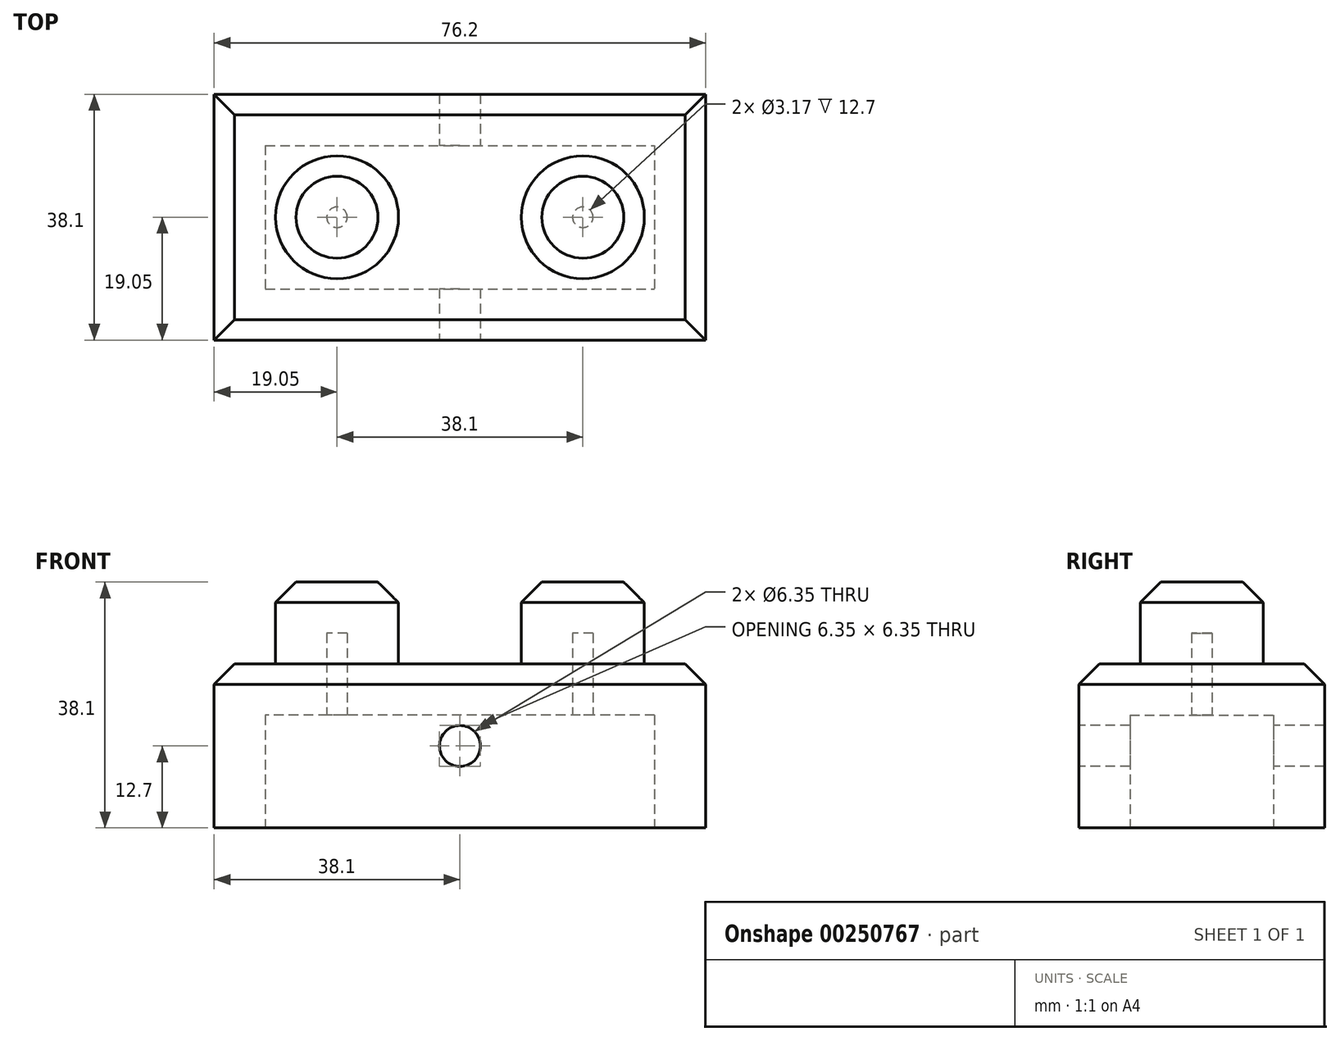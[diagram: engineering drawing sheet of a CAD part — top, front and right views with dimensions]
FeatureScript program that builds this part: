
annotation { "Feature Type Name" : "Feature", "Feature Type Description" : "" }
export const myFeature = defineFeature(function(context is Context, id is Id, definition is map)
    precondition{}
    {
        {
            var Q0;
            Q0=qCreatedBy(makeId("Top.planeOp"),FACE);
            var sketch = newSketch(context, id + "F0", { "sketchPlane" : qUnion([Q0])});
            skLineSegment(sketch, "E0.bottom", {"start": v(0, 0) * mm, "end": v(76.2, 0) * mm});
            skLineSegment(sketch, "E0.top", {"start": v(0, -38.1) * mm, "end": v(76.2, -38.1) * mm});
            skLineSegment(sketch, "E0.left", {"start": v(0, 0) * mm, "end": v(0, -38.1) * mm});
            skLineSegment(sketch, "E0.right", {"start": v(76.2, 0) * mm, "end": v(76.2, -38.1) * mm});
            skSolve(sketch);
        }
        {
            var Q0;
            Q0=makeQuery(id+"F0.imprint","IMPRINT",FACE,{"disambiguationData":[TD([[makeQuery(id+"F0.imprint","IMPRINT",EDGE,{"derivedFrom":sQuery(id+"F0.wireOp",EDGE,"E0.bottom")}),-1.0]])]});
            extrude(context, id + "F1", {"entities" : qUnion([Q0]), "depth" : 25.4 * mm});
        }
        {
            var Q0;
            Q0=makeQuery(id+"F1.opExtrude","CAP_FACE",FACE,{"disambiguationData":[OSD([sQuery(id+"F0.wireOp",EDGE,"E0.bottom"),sQuery(id+"F0.wireOp",EDGE,"E0.top"),sQuery(id+"F0.wireOp",EDGE,"E0.left"),sQuery(id+"F0.wireOp",EDGE,"E0.right")])],"isStart":false});
            var sketch = newSketch(context, id + "F2", { "sketchPlane" : qUnion([Q0])});
            skCircle(sketch, "E1", {"center": v(19.05, -19.05) * mm, "radius": 9.53 * mm});
            skCircle(sketch, "E2", {"center": v(57.15, -19.05) * mm, "radius": 9.53 * mm});
            skSolve(sketch);
        }
        {
            var Q0;
            Q0 = qSketchRegion(id + "F2", true);
            extrude(context, id + "F3", {"entities" : qUnion([Q0]), "operationType" : NewBodyOperationType.ADD, "depth" : 12.7 * mm});
        }
        {
            var Q0;
            Q0=makeQuery(id+"F3.opExtrude","CAP_EDGE",EDGE,{"disambiguationData":[OSD([sQuery(id+"F2.wireOp",EDGE,"E1")])],"isStart":false});
            var Q1;
            Q1=makeQuery(id+"F3.opExtrude","CAP_EDGE",EDGE,{"disambiguationData":[OSD([sQuery(id+"F2.wireOp",EDGE,"E2")])],"isStart":false});
            var Q2;
            Q2=makeQuery(id+"F1.opExtrude","CAP_EDGE",EDGE,{"disambiguationData":[OSD([sQuery(id+"F0.wireOp",EDGE,"E0.top")])],"isStart":false});
            var Q3;
            Q3=makeQuery(id+"F1.opExtrude","CAP_EDGE",EDGE,{"disambiguationData":[OSD([sQuery(id+"F0.wireOp",EDGE,"E0.right")])],"isStart":false});
            var Q4;
            Q4=makeQuery(id+"F1.opExtrude","CAP_EDGE",EDGE,{"disambiguationData":[OSD([sQuery(id+"F0.wireOp",EDGE,"E0.bottom")])],"isStart":false});
            var Q5;
            Q5=makeQuery(id+"F1.opExtrude","CAP_EDGE",EDGE,{"disambiguationData":[OSD([sQuery(id+"F0.wireOp",EDGE,"E0.left")])],"isStart":false});
            chamfer(context, id + "F4", {"entities" : qUnion([Q0, Q1, Q2, Q3, Q4, Q5]), "chamferType" : ChamferType.OFFSET_ANGLE, "width" : 3.17 * mm, "oppositeDirection" : false, "angle" : 45 * degree, "tangentPropagation" : true});
        }
        {
            var Q0;
            Q0=makeQuery(id+"F1.opExtrude","CAP_FACE",FACE,{"disambiguationData":[OSD([sQuery(id+"F0.wireOp",EDGE,"E0.bottom"),sQuery(id+"F0.wireOp",EDGE,"E0.top"),sQuery(id+"F0.wireOp",EDGE,"E0.left"),sQuery(id+"F0.wireOp",EDGE,"E0.right")])],"isStart":true});
            shell(context, id + "F5", {"entities" : qUnion([Q0]), "thickness" : 7.94 * mm});
        }
        {
            var Q0;
            Q0=makeQuery(id+"F1.opExtrude","SWEPT_FACE",FACE,{"disambiguationData":[OSD([sQuery(id+"F0.wireOp",EDGE,"E0.top")])]});
            var sketch = newSketch(context, id + "F6", { "sketchPlane" : qUnion([Q0])});
            skCircle(sketch, "E3", {"center": v(38.1, 12.7) * mm, "radius": 3.18 * mm});
            skSolve(sketch);
        }
        {
            var Q0;
            Q0 = qSketchRegion(id + "F6", true);
            extrude(context, id + "F7", {"entities" : qUnion([Q0]), "operationType" : NewBodyOperationType.REMOVE, "oppositeDirection" : true, "depth" : 38.1 * mm});
        }
    });
